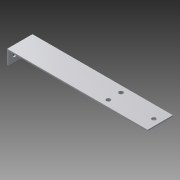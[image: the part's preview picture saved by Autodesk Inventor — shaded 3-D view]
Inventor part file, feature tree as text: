
AUTODESK INVENTOR PART (.ipt)
format: ipt  version: 2015 (Build 190159000, 159)  size: 131,072 bytes
history: native  units: mm
features: sketch x5, extrude x3, hole x2, other x1
ambient origin geometry x8: Origin, YZ Plane, XZ Plane, XY Plane, X Axis, Y Axis, Z Axis, Center Point
bodies: Body1 (feature_tree)
feature tree (11):
  other  "ソリッド1"
  extrude  "押し出し1"  Depth=120.0mm
  hole  "穴1"  [1 undecoded]
  extrude  "押し出し2"  Depth=1.0mm TaperAngle=0.0deg
  hole  "穴2"  [1 undecoded]
  extrude  "押し出し3"  Depth=10.0mm
  sketch  "スケッチ1"
  sketch  "スケッチ2"
  sketch  "スケッチ3"
  sketch  "スケッチ4"
  sketch  "スケッチ5"
note: 2 required parameter values undecoded (feature->parameter linkage not recoverable at this tier; creation-order binding heuristic only, values carry confidence <= 0.55)
